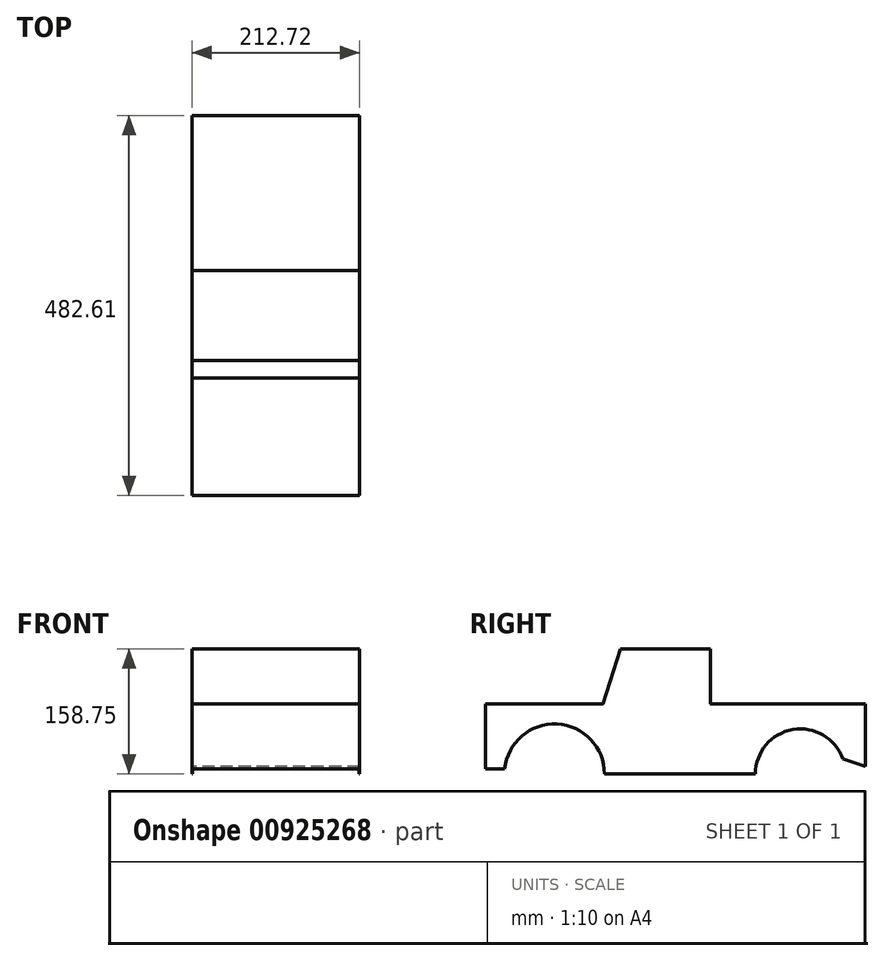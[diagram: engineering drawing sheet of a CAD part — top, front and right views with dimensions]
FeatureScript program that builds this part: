
annotation { "Feature Type Name" : "Feature", "Feature Type Description" : "" }
export const myFeature = defineFeature(function(context is Context, id is Id, definition is map)
    precondition{}
    {
        {
            var Q0;
            Q0=qCreatedBy(makeId("Right.planeOp"),FACE);
            var sketch = newSketch(context, id + "F0", { "sketchPlane" : qUnion([Q0])});
            skArc(sketch, "E0", {"start": v(-92.08, 0) * mm, "mid": v(-152.4, 63.42) * mm, "end": v(-218.76, 6.35) * mm});
            skArc(sketch, "E1", {"start": v(210.73, 19.05) * mm, "mid": v(147.18, 56.33) * mm, "end": v(99.7, 0) * mm});
            skLineSegment(sketch, "E2", {"start": v(-92.08, 0) * mm, "end": v(0, 0) * mm});
            skLineSegment(sketch, "E3", {"start": v(0, 0) * mm, "end": v(99.7, 0) * mm});
            skLineSegment(sketch, "E4", {"start": v(-243.2, 6.35) * mm, "end": v(-243.2, 88.9) * mm});
            skLineSegment(sketch, "E5", {"start": v(-243.2, 88.9) * mm, "end": v(-93.98, 88.9) * mm});
            skLineSegment(sketch, "E6", {"start": v(239.4, 9.53) * mm, "end": v(239.4, 88.9) * mm});
            skLineSegment(sketch, "E7", {"start": v(-93.98, 88.9) * mm, "end": v(-71.76, 158.75) * mm});
            skLineSegment(sketch, "E8", {"start": v(-71.76, 158.75) * mm, "end": v(42.54, 158.75) * mm});
            skLineSegment(sketch, "E9", {"start": v(42.54, 158.75) * mm, "end": v(42.55, 88.9) * mm});
            skLineSegment(sketch, "E10.trimOffspring", {"start": v(42.55, 88.9) * mm, "end": v(239.4, 88.9) * mm});
            skLineSegment(sketch, "E11", {"start": v(210.73, 19.05) * mm, "end": v(239.4, 9.53) * mm});
            skLineSegment(sketch, "E12", {"start": v(-218.76, 6.35) * mm, "end": v(-243.2, 6.35) * mm});
            skSolve(sketch);
        }
        {
            var Q0;
            Q0 = qSketchRegion(id + "F0", true);
            extrude(context, id + "F1", {"entities" : qUnion([Q0]), "endBound" : BoundingType.SYMMETRIC, "depth" : 212.72 * mm, "offsetDistance" : 25.4 * mm});
        }
        {
            var Q0;
            Q0=makeQuery(id+"F1.opExtrude","SWEPT_FACE",FACE,{"disambiguationData":[OSD([sQuery(id+"F0.wireOp",EDGE,"E2"),sQuery(id+"F0.wireOp",EDGE,"E3")])]});
            var Q1;
            Q1=makeQuery(id+"F1.opExtrude","SWEPT_FACE",FACE,{"disambiguationData":[OSD([sQuery(id+"F0.wireOp",EDGE,"E1")])]});
            var Q2;
            Q2=makeQuery(id+"F1.opExtrude","SWEPT_FACE",FACE,{"disambiguationData":[OSD([sQuery(id+"F0.wireOp",EDGE,"E11")])]});
            var Q3;
            Q3=makeQuery(id+"F1.opExtrude","SWEPT_FACE",FACE,{"disambiguationData":[OSD([sQuery(id+"F0.wireOp",EDGE,"E0")])]});
            var Q4;
            Q4=makeQuery(id+"F1.opExtrude","SWEPT_FACE",FACE,{"disambiguationData":[OSD([sQuery(id+"F0.wireOp",EDGE,"E12")])]});
            shell(context, id + "F2", {"entities" : qUnion([Q0, Q1, Q2, Q3, Q4]), "thickness" : 0.5 * mm});
        }
    });
